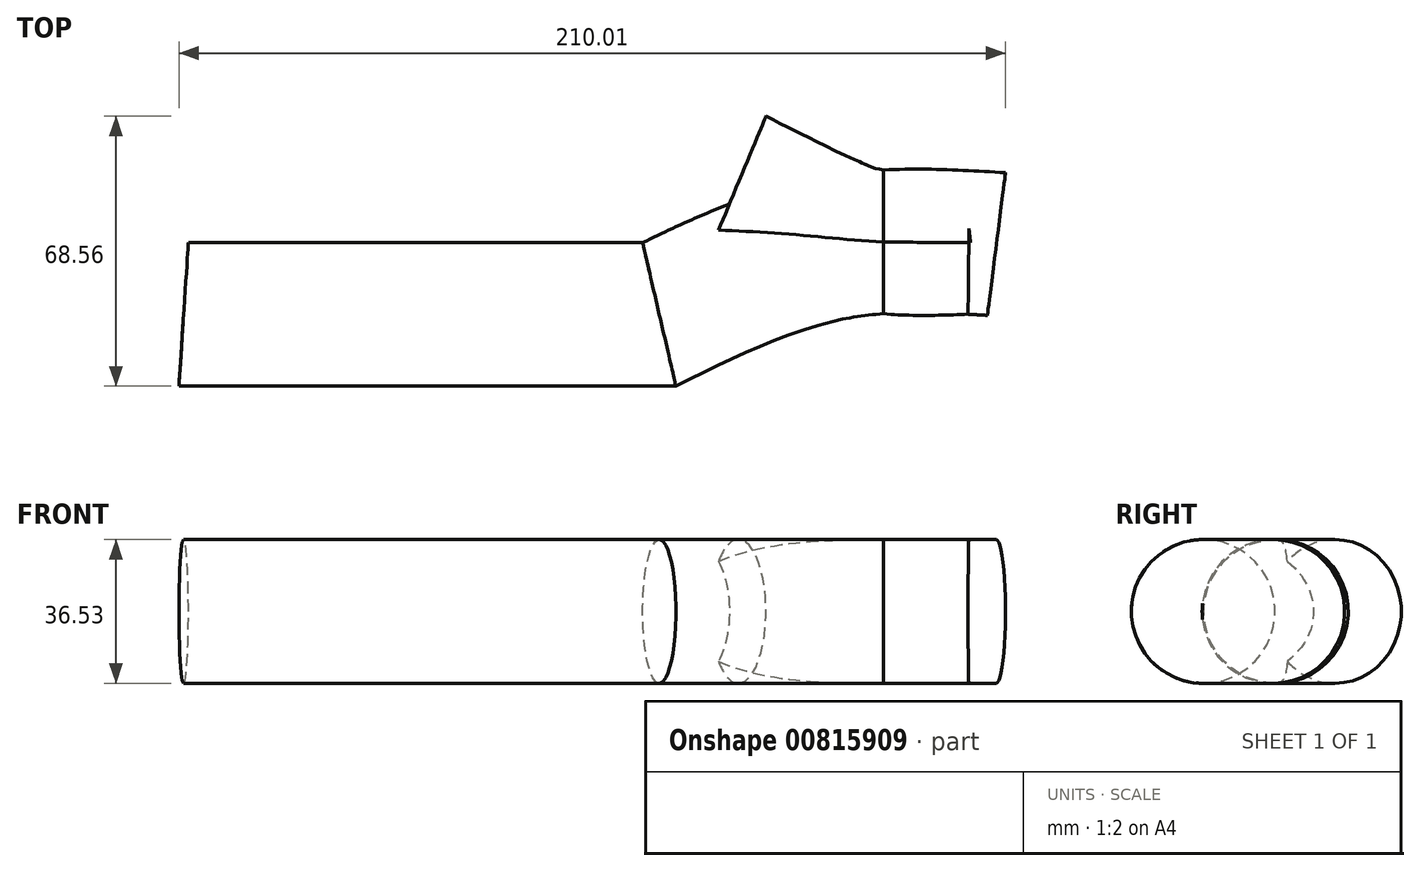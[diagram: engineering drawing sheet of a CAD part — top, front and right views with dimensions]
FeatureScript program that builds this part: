
annotation { "Feature Type Name" : "Feature", "Feature Type Description" : "" }
export const myFeature = defineFeature(function(context is Context, id is Id, definition is map)
    precondition{}
    {
        {
            var Q0;
            Q0=qCreatedBy(makeId("Top.planeOp"),FACE);
            var sketch = newSketch(context, id + "F0", { "sketchPlane" : qUnion([Q0])});
            skLineSegment(sketch, "E0", {"start": v(-178.43, 27.25) * mm, "end": v(-54.77, 27.25) * mm});
            skFitSpline(sketch, "E1", {"points": [v(-54.77, 27.25) * mm, v(-12.24, 44.03) * mm, v(27.5, 45.15) * mm], "startDerivative": vector(82.14, 40.23) * mm, "endDerivative": vector(82.38, -4.95) * mm});
            skFitSpline(sketch, "E2", {"points": [v(-54.77, 27.25) * mm, v(-13.36, 10.46) * mm, v(27.5, 8.78) * mm], "startDerivative": vector(80.37, -40.36) * mm, "endDerivative": vector(84.17, 3.76) * mm});
            skSolve(sketch);
        }
        {
            var Q0;
            Q0=qCreatedBy(makeId("Right.planeOp"),FACE);
            var sketch = newSketch(context, id + "F1", { "sketchPlane" : qUnion([Q0])});
            skCircle(sketch, "E3", {"center": v(55.17, 48.67) * mm, "radius": 18.26 * mm});
            skSolve(sketch);
        }
        {
            var Q0;
            Q0=makeQuery(id+"F1.imprint","IMPRINT",FACE,{"disambiguationData":[TD([[makeQuery(id+"F1.imprint","IMPRINT",EDGE,{"derivedFrom":sQuery(id+"F1.wireOp",EDGE,"E3")}),1.0]])]});
            var Q1;
            Q1=sQuery(id+"F0.wireOp",EDGE,"E0");
            var Q2;
            Q2=sQuery(id+"F0.wireOp",EDGE,"E1");
            sweep(context, id + "F2", {"profiles" : qUnion([Q0]), "path" : qUnion([Q1, Q2])});
        }
        {
            var Q0;
            Q0 = qSketchRegion(id + "F1", true);
            var Q1;
            Q1=sQuery(id+"F0.wireOp",EDGE,"E2");
            sweep(context, id + "F3", {"operationType" : NewBodyOperationType.ADD, "profiles" : qUnion([Q0]), "path" : qUnion([Q1])});
        }
    });
